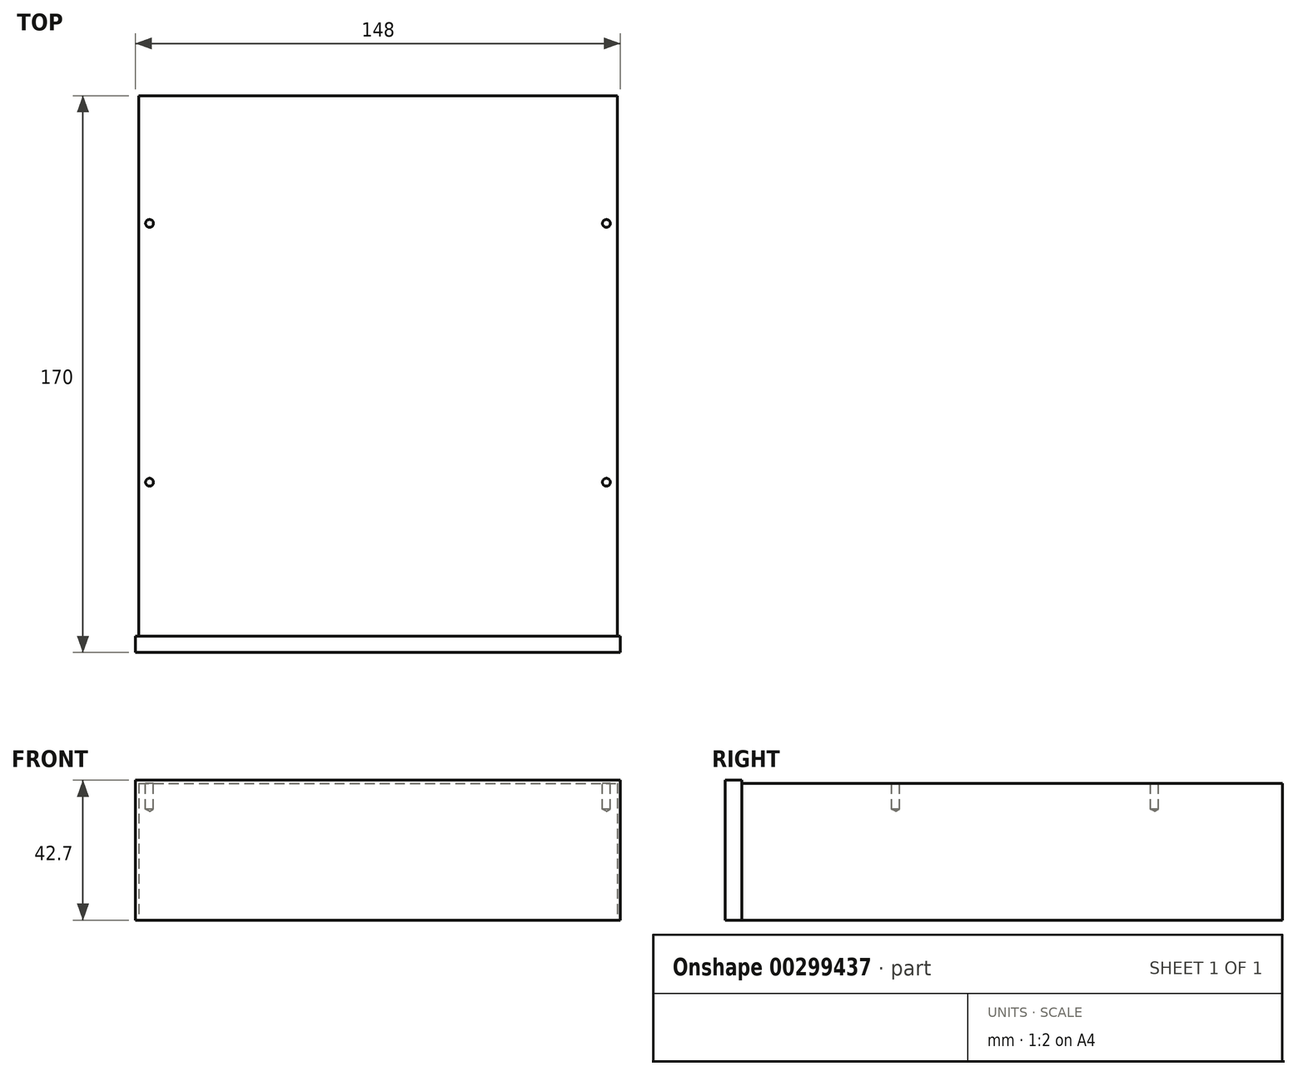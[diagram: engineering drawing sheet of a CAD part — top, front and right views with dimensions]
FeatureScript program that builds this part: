
annotation { "Feature Type Name" : "Feature", "Feature Type Description" : "" }
export const myFeature = defineFeature(function(context is Context, id is Id, definition is map)
    precondition{}
    {
        {
            var Q0;
            Q0=qCreatedBy(makeId("Top.planeOp"),FACE);
            var sketch = newSketch(context, id + "F0", { "sketchPlane" : qUnion([Q0])});
            skLineSegment(sketch, "E0.bottom", {"start": v(0, 0) * mm, "end": v(146, 0) * mm});
            skLineSegment(sketch, "E0.top", {"start": v(0, 165) * mm, "end": v(146, 165) * mm});
            skLineSegment(sketch, "E0.left", {"start": v(0, 0) * mm, "end": v(0, 165) * mm});
            skLineSegment(sketch, "E0.right", {"start": v(146, 0) * mm, "end": v(146, 165) * mm});
            skSolve(sketch);
        }
        {
            var Q0;
            Q0=makeQuery(id+"F0.imprint","IMPRINT",FACE,{"disambiguationData":[TD([[makeQuery(id+"F0.imprint","IMPRINT",EDGE,{"derivedFrom":sQuery(id+"F0.wireOp",EDGE,"E0.bottom")}),1.0]])]});
            extrude(context, id + "F1", {"entities" : qUnion([Q0]), "depth" : 41.7 * mm});
        }
        {
            var Q0;
            Q0=makeQuery(id+"F1.opExtrude","SWEPT_FACE",FACE,{"disambiguationData":[OSD([sQuery(id+"F0.wireOp",EDGE,"E0.bottom")])]});
            var sketch = newSketch(context, id + "F2", { "sketchPlane" : qUnion([Q0])});
            skLineSegment(sketch, "E1.bottom", {"start": v(-1, 42.7) * mm, "end": v(147, 42.7) * mm});
            skLineSegment(sketch, "E1.top", {"start": v(-1, 0) * mm, "end": v(147, 0) * mm});
            skLineSegment(sketch, "E1.left", {"start": v(-1, 42.7) * mm, "end": v(-1, 0) * mm});
            skLineSegment(sketch, "E1.right", {"start": v(147, 42.7) * mm, "end": v(147, 0) * mm});
            skSolve(sketch);
        }
        {
            var Q0;
            Q0 = qSketchRegion(id + "F2", true);
            extrude(context, id + "F3", {"entities" : qUnion([Q0]), "operationType" : NewBodyOperationType.ADD, "depth" : 5 * mm});
        }
        {
            var Q0;
            Q0=makeQuery(id+"F1.opExtrude","CAP_FACE",FACE,{"disambiguationData":[OSD([sQuery(id+"F0.wireOp",EDGE,"E0.bottom"),sQuery(id+"F0.wireOp",EDGE,"E0.top"),sQuery(id+"F0.wireOp",EDGE,"E0.left"),sQuery(id+"F0.wireOp",EDGE,"E0.right")])],"isStart":false});
            var sketch = newSketch(context, id + "F4", { "sketchPlane" : qUnion([Q0])});
            skLineSegment(sketch, "E2", {"start": v(0, 47) * mm, "end": v(146, 47) * mm, "construction": true});
            skLineSegment(sketch, "E3", {"start": v(0, 126) * mm, "end": v(146, 126) * mm, "construction": true});
            skLineSegment(sketch, "E4", {"start": v(3.3, 165) * mm, "end": v(3.3, 0) * mm, "construction": true});
            skLineSegment(sketch, "E5", {"start": v(142.7, 165) * mm, "end": v(142.7, 0) * mm, "construction": true});
            skPoint(sketch, "E6", {"position": v(3.3, 126) * mm});
            skPoint(sketch, "E7", {"position": v(142.7, 126) * mm});
            skPoint(sketch, "E8", {"position": v(142.7, 47) * mm});
            skPoint(sketch, "E9", {"position": v(3.3, 47) * mm});
            skSolve(sketch);
        }
        {
            var Q0;
            Q0=sQuery(id+"F4.wireOp",VERTEX,"E6");
            var Q1;
            Q1=sQuery(id+"F4.wireOp",VERTEX,"E7");
            var Q2;
            Q2=sQuery(id+"F4.wireOp",VERTEX,"E8");
            var Q3;
            Q3=sQuery(id+"F4.wireOp",VERTEX,"E9");
            var Q4;
            Q4=makeQuery(id+"F1.opExtrude","SWEPT_BODY",BODY,{"disambiguationData":[OSD([sQuery(id+"F0.wireOp",EDGE,"E0.bottom"),sQuery(id+"F0.wireOp",EDGE,"E0.top"),sQuery(id+"F0.wireOp",EDGE,"E0.left"),sQuery(id+"F0.wireOp",EDGE,"E0.right")])]});
            hole(context, id + "F5", {"style" : HoleStyle.SIMPLE, "endStyle" : HoleEndStyle.BLIND, "standardTappedOrClearance" : lookupTablePath({ "standard" : "ISO", "engagement" : "75%", "pitch" : "0.6 mm", "size" : "M3", "type" : "Tapped" }), "standardBlindInLast" : lookupTablePath({ "standard" : "ISO", "engagement" : "75%", "pitch" : "0.6 mm", "size" : "M3", "type" : "Tapped" }), "holeDiameter" : 2.4 * mm, "showTappedDepth" : true, "holeDepth" : 7.8 * mm, "tappedDepth" : 6 * mm, "tapClearance" : 3, "locations" : qUnion([Q0, Q1, Q2, Q3]), "scope" : qUnion([Q4])});
        }
    });
